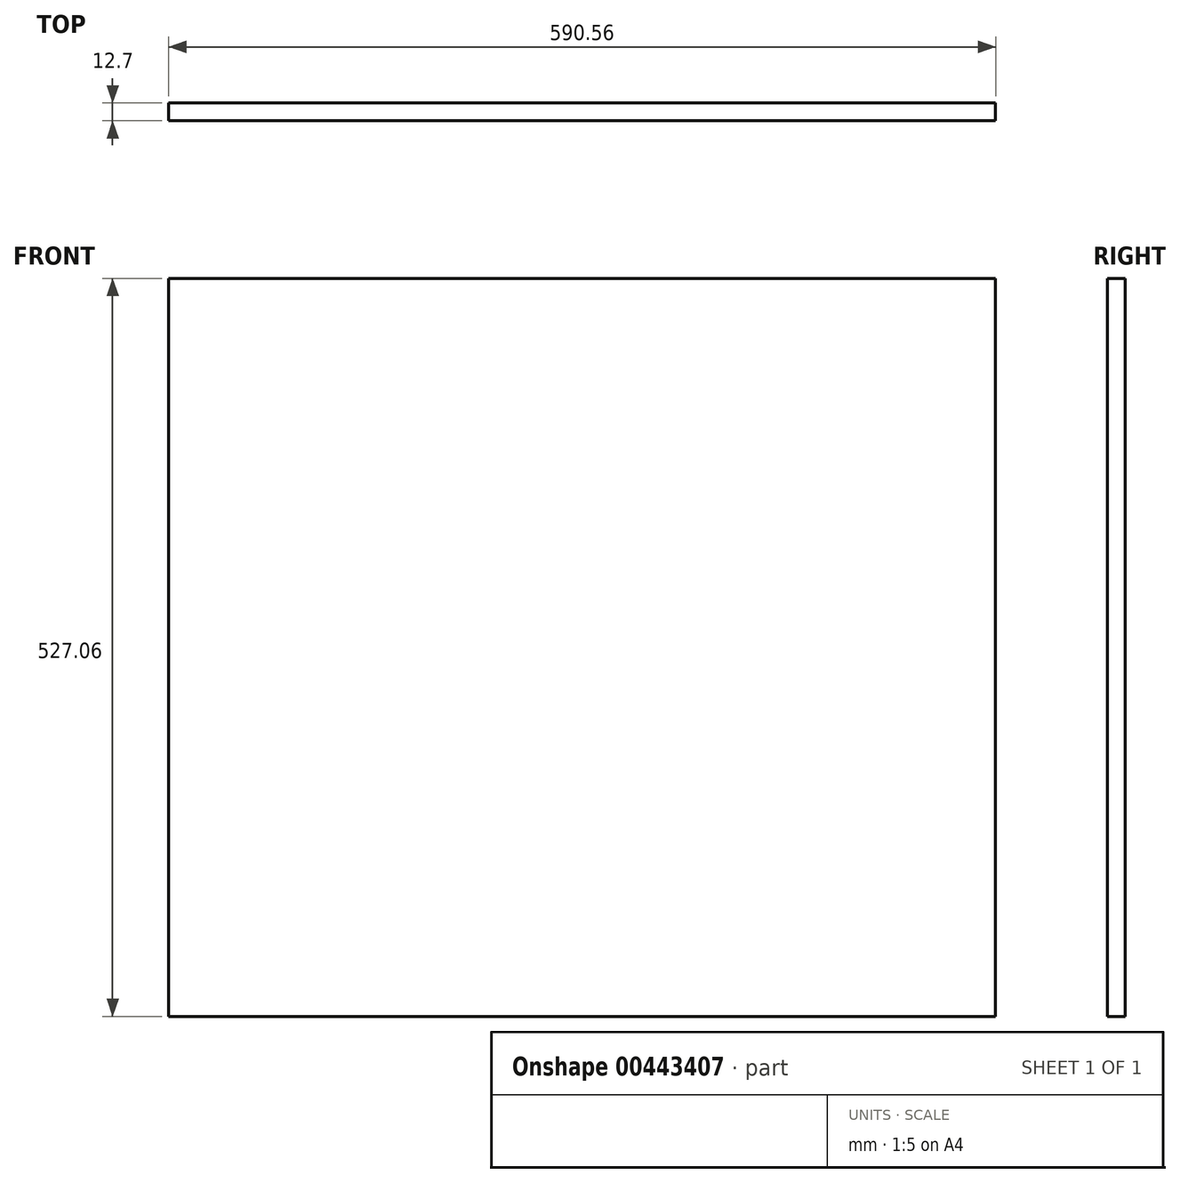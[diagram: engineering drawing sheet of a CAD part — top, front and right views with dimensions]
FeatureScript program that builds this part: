
annotation { "Feature Type Name" : "Feature", "Feature Type Description" : "" }
export const myFeature = defineFeature(function(context is Context, id is Id, definition is map)
    precondition{}
    {
        {
            var Q0;
            Q0=qCreatedBy(makeId("Front.planeOp"),FACE);
            var sketch = newSketch(context, id + "F0", { "sketchPlane" : qUnion([Q0])});
            skLineSegment(sketch, "E0.bottom", {"start": v(-295.27, 263.53) * mm, "end": v(295.28, 263.53) * mm});
            skLineSegment(sketch, "E0.top", {"start": v(-295.28, -263.53) * mm, "end": v(295.27, -263.53) * mm});
            skLineSegment(sketch, "E0.left", {"start": v(-295.27, 263.53) * mm, "end": v(-295.28, -263.53) * mm});
            skLineSegment(sketch, "E0.right", {"start": v(295.28, 263.53) * mm, "end": v(295.27, -263.53) * mm});
            skPoint(sketch, "E0.middle", {"position": v(0, 0) * mm});
            skSolve(sketch);
        }
        {
            var Q0;
            Q0 = qSketchRegion(id + "F0", true);
            extrude(context, id + "F1", {"entities" : qUnion([Q0]), "depth" : 12.7 * mm});
        }
    });
